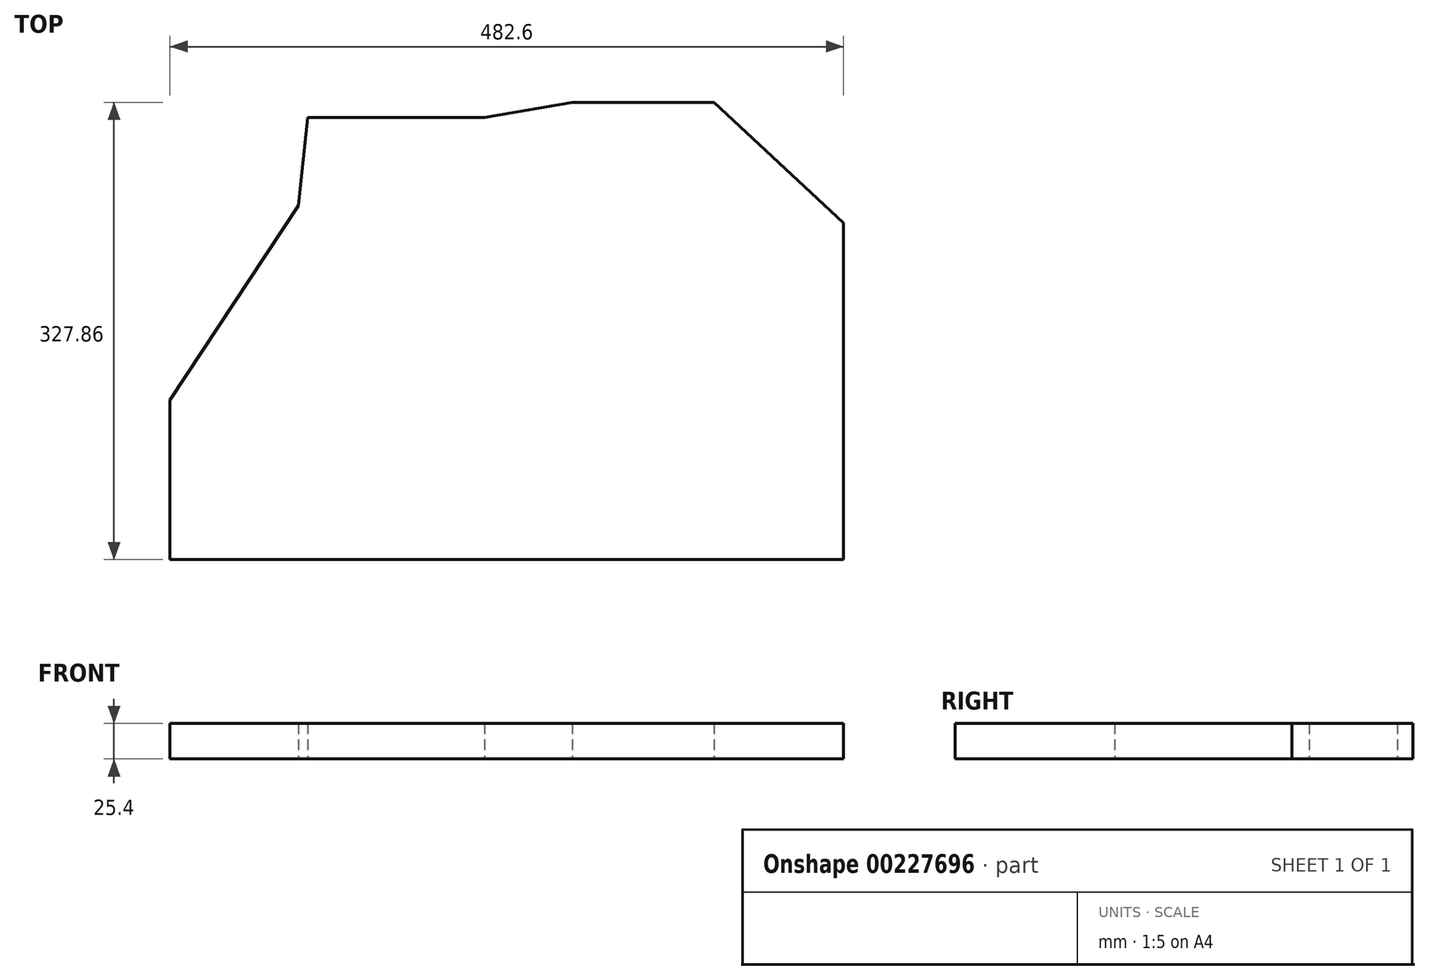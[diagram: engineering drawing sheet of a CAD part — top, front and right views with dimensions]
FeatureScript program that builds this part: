
annotation { "Feature Type Name" : "Feature", "Feature Type Description" : "" }
export const myFeature = defineFeature(function(context is Context, id is Id, definition is map)
    precondition{}
    {
        {
            var Q0;
            Q0=qCreatedBy(makeId("Top.planeOp"),FACE);
            var sketch = newSketch(context, id + "F0", { "sketchPlane" : qUnion([Q0])});
            skLineSegment(sketch, "E0", {"start": v(166.7, 198.54) * mm, "end": v(166.7, -42.76) * mm});
            skLineSegment(sketch, "E1", {"start": v(166.7, -42.76) * mm, "end": v(-315.9, -42.76) * mm});
            skLineSegment(sketch, "E2", {"start": v(-315.9, 71.54) * mm, "end": v(-223.92, 210.91) * mm});
            skLineSegment(sketch, "E3", {"start": v(-223.92, 210.91) * mm, "end": v(-217.36, 274.07) * mm});
            skLineSegment(sketch, "E4", {"start": v(-90.36, 274.07) * mm, "end": v(-27.83, 285.1) * mm});
            skLineSegment(sketch, "E5", {"start": v(73.77, 285.1) * mm, "end": v(166.7, 198.54) * mm});
            skLineSegment(sketch, "E6", {"start": v(73.77, 285.1) * mm, "end": v(-27.83, 285.1) * mm});
            skLineSegment(sketch, "E7", {"start": v(-90.36, 274.07) * mm, "end": v(-217.36, 274.07) * mm});
            skLineSegment(sketch, "E8", {"start": v(-186.78, 274.07) * mm, "end": v(-143.04, 274.07) * mm});
            skLineSegment(sketch, "E9", {"start": v(-90.36, 274.07) * mm, "end": v(-143.04, 274.07) * mm});
            skLineSegment(sketch, "E10", {"start": v(-143.04, 274.07) * mm, "end": v(-148.6, 274.07) * mm});
            skLineSegment(sketch, "E11", {"start": v(-315.9, 71.54) * mm, "end": v(-315.9, -42.76) * mm});
            skLineSegment(sketch, "E12", {"start": v(-315.9, 71.54) * mm, "end": v(-311.23, 94.8) * mm});
            skSolve(sketch);
        }
        {
            var Q0;
            Q0=makeQuery(id+"F0.imprint","IMPRINT",FACE,{"disambiguationData":[TD([[makeQuery(id+"F0.imprint","IMPRINT",EDGE,{"derivedFrom":sQuery(id+"F0.wireOp",EDGE,"E0")}),-1.0]])]});
            extrude(context, id + "F1", {"entities" : qUnion([Q0]), "depth" : 25.4 * mm});
        }
    });
